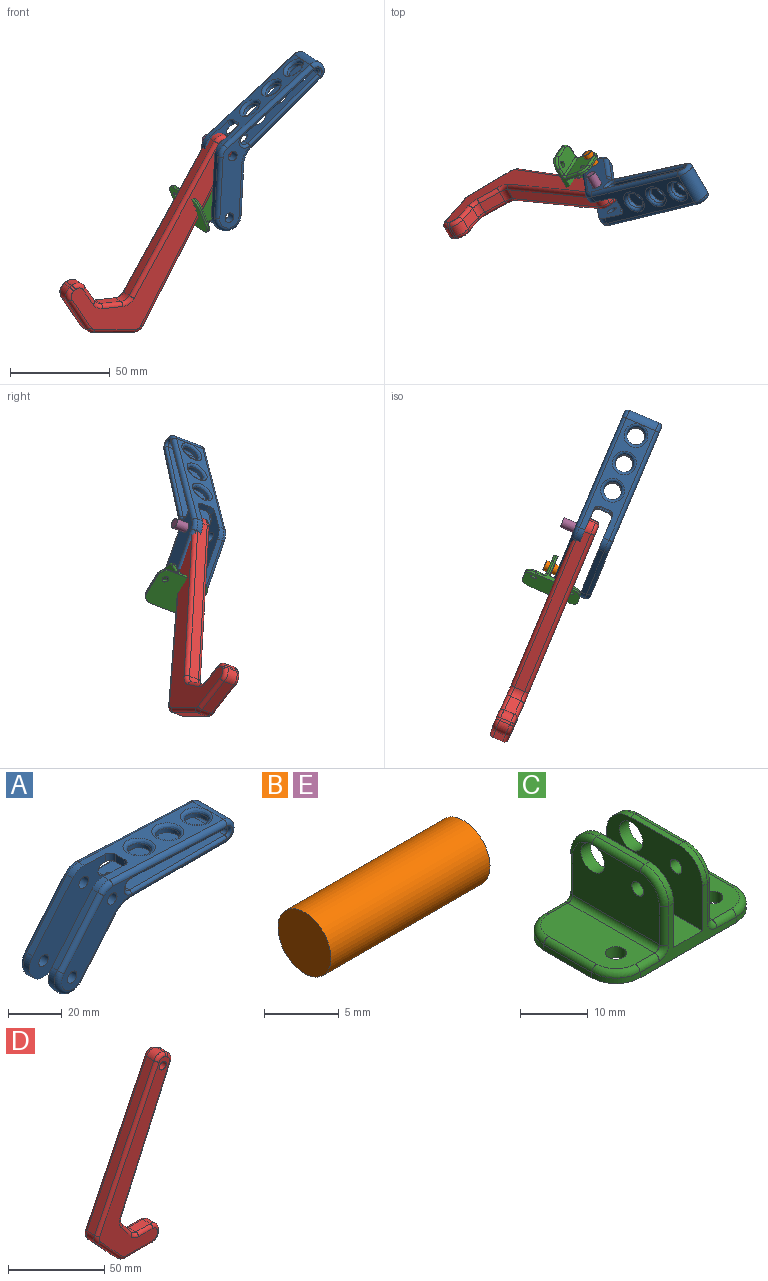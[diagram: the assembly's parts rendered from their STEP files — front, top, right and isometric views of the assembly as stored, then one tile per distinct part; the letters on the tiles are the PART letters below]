
ASSEMBLY  parts=5 mates=4
PART A: 69 faces, bbox 94.6x20x41.3 mm
  f0: plane 89.48x36mm, normal (0,-1,0), area 446.6mm2, adj f11,f13,f35,f36,f37,f38,f39,f40
  f1: plane 89.48x36mm, normal (0,1,0), area 446.6mm2, adj f21,f23,f27,f28,f29,f30,f31,f32
  f2: plane 5x3.37mm, normal (-1,0,0.04), area 16.9mm2, adj f5,f6,f16,f45
  f3: plane 40.19x40mm, normal (0,-1,0), area 673.6mm2, adj f5,f14,f16,f17,f18,f19,f20,f21
  f4: plane 40.19x40mm, normal (0,1,0), area 673.6mm2, adj f6,f7,f8,f9,f10,f11,f12,f13
  f5: cylinder r=2.5mm len=3.47mm, axis (0.04,0,1), area 13.2mm2, adj f2,f3,f16,f45
  f6: cylinder r=2.5mm len=3.47mm, axis (-0.04,0,-1), area 13.2mm2, adj f2,f4,f16,f45
  f7: cylinder r=7.5mm len=6.06mm, axis (0,1,0), area 20.6mm2, adj f4,f8,f16,f40
  f8: plane 25x20.98mm, normal (-0.77,0,0.64), area 97.9mm2, adj f4,f7,f9,f42
  f9: cylinder r=7.5mm len=13.25mm, axis (0,1,0), area 70.7mm2, adj f4,f8,f10,f41
  f10: plane 21.25x17.82mm, normal (0.77,0,-0.64), area 83.2mm2, adj f4,f9,f12,f39
  f11: cylinder r=2.5mm len=5mm, axis (0,1,0), area 78.5mm2, adj f0,f4
  f12: cylinder r=10mm len=7.66mm, axis (0,1,0), area 26.2mm2, adj f4,f10,f14,f37
  f13: cylinder r=2.5mm len=5mm, axis (0,1,0), area 78.5mm2, adj f0,f4
  f14: plane 49.79x16.04mm, normal (0,0,-1), area 424.8mm2, adj f3,f4,f12,f15,f22,f24,f25,f26
  f15: cylinder r=5mm len=16mm, axis (0,1,0), area 247.9mm2, adj f14,f16,f33,f36,f66
  f16: plane 59.9x16mm, normal (0.04,0,1), area 483.2mm2, adj f2,f3,f4,f5,f6,f7,f15,f17
  f17: cylinder r=7.5mm len=6.06mm, axis (0,1,0), area 20.6mm2, adj f3,f16,f18,f29
  f18: plane 25x20.98mm, normal (-0.77,0,0.64), area 97.9mm2, adj f3,f17,f19,f27
  f19: cylinder r=7.5mm len=13.25mm, axis (0,1,0), area 70.7mm2, adj f3,f18,f20,f28
  f20: plane 21.25x17.82mm, normal (0.77,0,-0.64), area 83.2mm2, adj f3,f19,f22,f30
  f21: cylinder r=2.5mm len=5mm, axis (0,1,0), area 78.5mm2, adj f1,f3
  f22: cylinder r=10mm len=7.66mm, axis (0,1,0), area 26.2mm2, adj f3,f14,f20,f32
  f23: cylinder r=2.5mm len=5mm, axis (0,1,0), area 78.5mm2, adj f1,f3
  f24: plane 5x3.37mm, normal (-1,0,0.04), area 16.9mm2, adj f14,f25,f26,f46
  f25: cylinder r=2.5mm len=3.58mm, axis (0.04,0,1), area 13.2mm2, adj f3,f14,f24,f46
  f26: cylinder r=2.5mm len=3.58mm, axis (-0.04,0,-1), area 13.2mm2, adj f4,f14,f24,f46
  f27: cylinder r=2mm len=26.29mm, axis (-0.64,0,-0.77), area 102.5mm2, adj f1,f18,f28,f29
  f28: torus R=5.5mm, axis (0,-1,0), area 66.9mm2, adj f1,f19,f27,f30
  f29: torus R=5.5mm, axis (0,-1,0), area 19.5mm2, adj f1,f17,f27,f31
  f30: cylinder r=2mm len=22.53mm, axis (0.64,0,0.77), area 87.1mm2, adj f1,f20,f28,f32
  f31: cylinder r=2mm len=59.98mm, axis (-1,0,0.04), area 188.3mm2, adj f1,f16,f29,f33
  f32: torus R=12mm, axis (0,-1,0), area 29.4mm2, adj f1,f22,f30,f34
  f33: torus R=3mm, axis (0,-1,0), area 41.6mm2, adj f1,f15,f31,f34
  f34: cylinder r=2mm len=49.75mm, axis (1,0,0), area 156.3mm2, adj f1,f14,f32,f33
  f35: cylinder r=2mm len=49.75mm, axis (-1,0,0), area 156.3mm2, adj f0,f14,f36,f37
  f36: torus R=3mm, axis (0,-1,0), area 41.6mm2, adj f0,f15,f35,f38
  f37: torus R=12mm, axis (0,-1,0), area 29.4mm2, adj f0,f12,f35,f39
  f38: cylinder r=2mm len=59.98mm, axis (1,0,-0.04), area 188.3mm2, adj f0,f16,f36,f40
  f39: cylinder r=2mm len=22.53mm, axis (-0.64,0,-0.77), area 87.1mm2, adj f0,f10,f37,f41
  f40: torus R=5.5mm, axis (0,-1,0), area 19.5mm2, adj f0,f7,f38,f42
  f41: torus R=5.5mm, axis (0,-1,0), area 66.9mm2, adj f0,f9,f39,f42
  f42: cylinder r=2mm len=26.29mm, axis (0.64,0,0.77), area 102.5mm2, adj f0,f8,f40,f41
  f43: cylinder r=1.63mm len=17.4mm, axis (0,-1,0), area 87.9mm2, adj f45,f46,f51,f54
  f44: cylinder r=2.67mm len=5.34mm, axis (0,-1,0), area 31.4mm2, adj f3,f45,f46,f48
  f45: plane 49.81x17.4mm, normal (-0.04,0,-1), area 641mm2, adj f2,f3,f4,f5,f6,f43,f44,f47
  f46: plane 49.9x17.44mm, normal (0,0,1), area 642.2mm2, adj f3,f4,f24,f25,f26,f43,f44,f47
  f47: cylinder r=2.67mm len=5.34mm, axis (0,-1,0), area 31.4mm2, adj f4,f45,f46,f53
  f48: torus R=3.97mm, axis (0,-1,0), area 20.4mm2, adj f1,f44,f49,f50
  f49: cylinder r=1.3mm len=49.86mm, axis (1,0,0), area 101.8mm2, adj f1,f46,f48,f51
  f50: cylinder r=1.3mm len=49.87mm, axis (-1,0,0.04), area 101.8mm2, adj f1,f45,f48,f51
  f51: torus R=2.93mm, axis (0,-1,0), area 13.3mm2, adj f1,f43,f49,f50
  f52: cylinder r=1.3mm len=49.87mm, axis (1,0,-0.04), area 101.8mm2, adj f0,f45,f53,f54
  f53: torus R=3.97mm, axis (0,-1,0), area 20.4mm2, adj f0,f47,f52,f55
  f54: torus R=2.93mm, axis (0,-1,0), area 13.3mm2, adj f0,f43,f52,f55
  f55: cylinder r=1.3mm len=49.86mm, axis (-1,0,0), area 101.8mm2, adj f0,f46,f53,f54
  f56: cylinder r=4.5mm len=9mm, axis (0,0,-1), area 52.9mm2, adj f46,f65,f66
  f57: cylinder r=4.5mm len=9mm, axis (0,0,-1), area 52.9mm2, adj f46,f67
  f58: cylinder r=4.5mm len=9mm, axis (0,0,-1), area 52.9mm2, adj f46,f68
  f59: cylinder r=4.5mm len=9mm, axis (0,0,-1), area 52.9mm2, adj f45,f64
  f60: cylinder r=4.5mm len=9mm, axis (0,0,-1), area 52.9mm2, adj f45,f63
  f61: cylinder r=4.5mm len=9mm, axis (0,0,-1), area 52.9mm2, adj f45,f62
  f62: bspline ~12x12mm, area 74.7mm2, adj f16,f61
  f63: bspline ~11.99x11.99mm, area 74.7mm2, adj f16,f60
  f64: bspline ~11.99x11.99mm, area 74.7mm2, adj f16,f59
  f65: torus R=6mm, axis (0,0,1), area 71.5mm2, adj f14,f56,f66
  f66: bspline ~3.89x1.77mm, area 3.2mm2, adj f15,f56,f65
  f67: torus R=6mm, axis (0,0,1), area 74.7mm2, adj f14,f57
  f68: torus R=6mm, axis (0,0,1), area 74.7mm2, adj f14,f58
PART B: 3 faces, bbox 15x5x5 mm
  f0: cylinder r=2.5mm len=15mm, axis (-1,0,0), area 235.6mm2, adj f1,f2
  f1: plane 5x5mm, normal (1,0,0), area 19.6mm2, adj f0
  f2: plane 5x5mm, normal (-1,0,0), area 19.6mm2, adj f0
PART C: 54 faces, bbox 30.8x20.8x15.4 mm
  f0: plane 18x8mm, normal (0,0,1), area 129.1mm2, adj f24,f25,f26,f27,f28,f29,f51
  f1: plane 10x1mm, normal (-1,0,0), area 10mm2, adj f2,f21,f23,f24
  f2: plane 30x20mm, normal (0,0,-1), area 562.5mm2, adj f1,f3,f12,f13,f20,f21,f22,f23
  f3: plane 10x1mm, normal (1,0,0), area 10mm2, adj f2,f20,f22,f37
  f4: plane 18x8mm, normal (0,0,1), area 129.1mm2, adj f37,f38,f39,f40,f41,f42,f50
  f5: plane 18x11mm, normal (1,0,0), area 167.9mm2, adj f15,f42,f45,f46,f47,f48,f49,f53
  f6: plane 10x1mm, normal (0,0,1), area 10mm2, adj f7,f17,f19,f49
  f7: plane 20x13mm, normal (-1,0,0), area 225.9mm2, adj f6,f8,f12,f13,f15,f17,f19,f53
  f8: plane 20x6mm, normal (0,0,1), area 120mm2, adj f7,f9,f12,f13
  f9: plane 20x13mm, normal (1,0,0), area 225.9mm2, adj f8,f10,f12,f13,f14,f16,f18,f52
  f10: plane 10x1mm, normal (0,0,1), area 10mm2, adj f9,f16,f18,f36
  f11: plane 18x11mm, normal (-1,0,0), area 167.9mm2, adj f14,f28,f32,f33,f34,f35,f36,f52
  f12: plane 20x10mm, normal (0,-1,0), area 45.7mm2, adj f2,f7,f8,f9,f16,f17,f22,f23
  f13: plane 20x10mm, normal (0,1,0), area 45.7mm2, adj f2,f7,f8,f9,f18,f19,f20,f21
  f14: cylinder r=2.45mm len=4.9mm, axis (-1,0,0), area 30.8mm2, adj f9,f11,f35,f36
  f15: cylinder r=2.45mm len=4.9mm, axis (-1,0,0), area 30.8mm2, adj f5,f7,f48,f49
  f16: cylinder r=5mm len=5mm, axis (1,0,0), area 7.9mm2, adj f9,f10,f12,f34
  f17: cylinder r=5mm len=5mm, axis (1,0,0), area 7.9mm2, adj f6,f7,f12,f47
  f18: cylinder r=5mm len=5mm, axis (-1,0,0), area 7.9mm2, adj f9,f10,f13,f35
  f19: cylinder r=5mm len=5mm, axis (-1,0,0), area 7.9mm2, adj f6,f7,f13,f48
  f20: cylinder r=5mm len=5mm, axis (0,0,1), area 7.9mm2, adj f2,f3,f13,f39
  f21: cylinder r=5mm len=5mm, axis (0,0,-1), area 7.9mm2, adj f1,f2,f13,f26
  f22: cylinder r=5mm len=5mm, axis (0,0,-1), area 7.9mm2, adj f2,f3,f12,f38
  f23: cylinder r=5mm len=5mm, axis (0,0,1), area 7.9mm2, adj f1,f2,f12,f25
  f24: cylinder r=1mm len=10mm, axis (0,1,0), area 15.7mm2, adj f0,f1,f25,f26
  f25: torus R=4mm, axis (0,0,1), area 11.4mm2, adj f0,f23,f24,f27
  f26: torus R=4mm, axis (0,0,1), area 11.4mm2, adj f0,f21,f24,f29
  f27: cylinder r=1mm len=4mm, axis (1,0,0), area 6.3mm2, adj f0,f12,f25,f30
  f28: cylinder r=1mm len=18mm, axis (0,-1,0), area 28.3mm2, adj f0,f11,f30,f31
  f29: cylinder r=1mm len=4mm, axis (-1,0,0), area 6.3mm2, adj f0,f13,f26,f31
  f30: torus R=2mm, axis (0,-1,0), area 3.4mm2, adj f12,f27,f28,f32
  f31: torus R=2mm, axis (0,-1,0), area 3.4mm2, adj f13,f28,f29,f33
  f32: cylinder r=1mm len=7mm, axis (0,0,1), area 11mm2, adj f11,f12,f30,f34
  f33: cylinder r=1mm len=7mm, axis (0,0,-1), area 11mm2, adj f11,f13,f31,f35
  f34: torus R=4mm, axis (-1,0,0), area 11.4mm2, adj f11,f16,f32,f36
  f35: torus R=4mm, axis (-1,0,0), area 11.4mm2, adj f11,f14,f18,f33,f36
  f36: cylinder r=1mm len=10mm, axis (0,1,0), area 15.6mm2, adj f10,f11,f14,f34,f35
  f37: cylinder r=1mm len=10mm, axis (0,1,0), area 15.7mm2, adj f3,f4,f38,f39
  f38: torus R=4mm, axis (0,0,-1), area 11.4mm2, adj f4,f22,f37,f40
  f39: torus R=4mm, axis (0,0,-1), area 11.4mm2, adj f4,f20,f37,f41
  f40: cylinder r=1mm len=4mm, axis (1,0,0), area 6.3mm2, adj f4,f12,f38,f43
  f41: cylinder r=1mm len=4mm, axis (-1,0,0), area 6.3mm2, adj f4,f13,f39,f44
  f42: cylinder r=1mm len=18mm, axis (0,-1,0), area 28.3mm2, adj f4,f5,f43,f44
  f43: torus R=2mm, axis (0,-1,0), area 3.4mm2, adj f12,f40,f42,f45
  f44: torus R=2mm, axis (0,-1,0), area 3.4mm2, adj f13,f41,f42,f46
  f45: cylinder r=1mm len=7mm, axis (0,0,-1), area 11mm2, adj f5,f12,f43,f47
  f46: cylinder r=1mm len=7mm, axis (0,0,1), area 11mm2, adj f5,f13,f44,f48
  f47: torus R=4mm, axis (-1,0,0), area 11.4mm2, adj f5,f17,f45,f49
  f48: torus R=4mm, axis (-1,0,0), area 11.4mm2, adj f5,f15,f19,f46,f49
  f49: cylinder r=1mm len=10mm, axis (0,1,0), area 15.6mm2, adj f5,f6,f15,f47,f48
  f50: cylinder r=1.6mm len=3.2mm, axis (0,0,-1), area 20.1mm2, adj f2,f4
  f51: cylinder r=1.6mm len=3.2mm, axis (0,0,-1), area 20.1mm2, adj f0,f2
  f52: cylinder r=1.2mm len=2.4mm, axis (1,0,0), area 15.1mm2, adj f9,f11
  f53: cylinder r=1.2mm len=2.4mm, axis (1,0,0), area 15.1mm2, adj f5,f7
PART D: 51 faces, bbox 56.5x9.5x117.6 mm
  f0: plane 5.5x1.43mm, normal (1,0,0), area 7.9mm2, adj f1,f16,f30,f49
  f1: cylinder r=5.08mm len=5.5mm, axis (0,1,0), area 43.9mm2, adj f0,f2,f32,f47
  f2: plane 10.53x5.5mm, normal (0,0,1), area 57.9mm2, adj f1,f3,f34,f45
  f3: cylinder r=5.08mm len=5.5mm, axis (0,1,0), area 25.6mm2, adj f2,f4,f33,f43
  f4: plane 9.18x7.03mm, normal (0.79,0,0.61), area 63.6mm2, adj f3,f5,f31,f41
  f5: cylinder r=5.08mm len=5.5mm, axis (0,1,0), area 30mm2, adj f4,f6,f29,f39
  f6: plane 80.63x36.01mm, normal (0.91,0,-0.41), area 485.7mm2, adj f5,f7,f27,f37
  f7: cylinder r=5.08mm len=6.48mm, axis (0,1,0), area 41.1mm2, adj f6,f8,f25,f35
  f8: plane 5.5x1.91mm, normal (0.5,0,0.87), area 12.1mm2, adj f7,f9,f23,f36
  f9: cylinder r=5.08mm len=7.1mm, axis (0,1,0), area 45.8mm2, adj f8,f10,f21,f38
  f10: plane 89.34x43.6mm, normal (-0.9,0,0.44), area 546.7mm2, adj f9,f11,f19,f40
  f11: cylinder r=5.08mm len=5.69mm, axis (0,1,0), area 33.6mm2, adj f10,f12,f20,f42
  f12: plane 17.31x16.12mm, normal (-0.73,0,-0.68), area 130.1mm2, adj f11,f13,f22,f44
  f13: cylinder r=5.08mm len=5.5mm, axis (0,1,0), area 22.9mm2, adj f12,f14,f24,f46
  f14: plane 20.22x5.5mm, normal (0,0,-1), area 111.2mm2, adj f13,f16,f26,f48
  f15: cylinder r=2.5mm len=9.5mm, axis (0,1,0), area 149.2mm2, adj f17,f18
  f16: cylinder r=5.08mm len=5.5mm, axis (0,1,0), area 43.9mm2, adj f0,f14,f28,f50
  f17: plane 112.81x51.67mm, normal (0,-1,0), area 1401.9mm2, adj f15,f19,f20,f21,f22,f23,f24,f25
  f18: plane 112.81x51.67mm, normal (0,1,0), area 1401.9mm2, adj f15,f35,f36,f37,f38,f39,f40,f41
  f19: cylinder r=2mm len=90.22mm, axis (0.44,0,0.9), area 312.3mm2, adj f10,f17,f20,f21
  f20: torus R=3.08mm, axis (0,-1,0), area 16.5mm2, adj f11,f17,f19,f22
  f21: torus R=3.08mm, axis (0,-1,0), area 22.4mm2, adj f9,f17,f19,f23
  f22: cylinder r=2mm len=18.67mm, axis (-0.68,0,0.73), area 74.3mm2, adj f12,f17,f20,f24
  f23: cylinder r=2mm len=2.91mm, axis (0.87,0,-0.5), area 6.9mm2, adj f8,f17,f21,f25
  f24: torus R=3.08mm, axis (0,-1,0), area 11.2mm2, adj f13,f17,f22,f26
  f25: torus R=3.08mm, axis (0,-1,0), area 20.1mm2, adj f7,f17,f23,f27
  f26: cylinder r=2mm len=20.22mm, axis (-1,0,0), area 63.5mm2, adj f14,f17,f24,f28
  f27: cylinder r=2mm len=81.45mm, axis (-0.41,0,-0.91), area 277.4mm2, adj f6,f17,f25,f29
  f28: torus R=3.08mm, axis (0,-1,0), area 21.5mm2, adj f16,f17,f26,f30
  f29: torus R=7.08mm, axis (0,-1,0), area 19.6mm2, adj f5,f17,f27,f31
  f30: cylinder r=2mm len=2mm, axis (0,0,-1), area 4.5mm2, adj f0,f17,f28,f32
  f31: cylinder r=2mm len=10.4mm, axis (0.61,0,-0.79), area 36.3mm2, adj f4,f17,f29,f33
  f32: torus R=3.08mm, axis (0,-1,0), area 21.5mm2, adj f1,f17,f30,f34
  f33: torus R=7.08mm, axis (0,-1,0), area 16.7mm2, adj f3,f17,f31,f34
  f34: cylinder r=2mm len=10.53mm, axis (1,0,0), area 33.1mm2, adj f2,f17,f32,f33
  f35: torus R=3.08mm, axis (0,-1,0), area 20.1mm2, adj f7,f18,f36,f37
  f36: cylinder r=2mm len=2.91mm, axis (-0.87,0,0.5), area 6.9mm2, adj f8,f18,f35,f38
  f37: cylinder r=2mm len=81.45mm, axis (0.41,0,0.91), area 277.4mm2, adj f6,f18,f35,f39
  f38: torus R=3.08mm, axis (0,-1,0), area 22.4mm2, adj f9,f18,f36,f40
  f39: torus R=7.08mm, axis (0,-1,0), area 19.6mm2, adj f5,f18,f37,f41
  f40: cylinder r=2mm len=90.22mm, axis (-0.44,0,-0.9), area 312.3mm2, adj f10,f18,f38,f42
  f41: cylinder r=2mm len=10.4mm, axis (-0.61,0,0.79), area 36.3mm2, adj f4,f18,f39,f43
  f42: torus R=3.08mm, axis (0,-1,0), area 16.5mm2, adj f11,f18,f40,f44
  f43: torus R=7.08mm, axis (0,-1,0), area 16.7mm2, adj f3,f18,f41,f45
  f44: cylinder r=2mm len=18.67mm, axis (0.68,0,-0.73), area 74.3mm2, adj f12,f18,f42,f46
  f45: cylinder r=2mm len=10.53mm, axis (-1,0,0), area 33.1mm2, adj f2,f18,f43,f47
  f46: torus R=3.08mm, axis (0,-1,0), area 11.2mm2, adj f13,f18,f44,f48
  f47: torus R=3.08mm, axis (0,-1,0), area 21.5mm2, adj f1,f18,f45,f49
  f48: cylinder r=2mm len=20.22mm, axis (1,0,0), area 63.5mm2, adj f14,f18,f46,f50
  f49: cylinder r=2mm len=2mm, axis (0,0,1), area 4.5mm2, adj f0,f18,f47,f50
  f50: torus R=3.08mm, axis (0,-1,0), area 21.5mm2, adj f16,f18,f48,f49
PART E: same geometry as B
PLACE A rot(axis=(0.53,-0.75,0.39),54.3deg) t=(63.62,-98.37,-16.55)mm
PLACE B rot(axis=(-0.56,0.58,-0.59),75.8deg) t=(27.81,-92.15,-66.07)mm
PLACE C rot(axis=(-0.56,0.58,-0.59),75.8deg) t=(33.11,-102.18,-55.39)mm
PLACE D rot(axis=(-0.44,0.04,-0.9),145.1deg) t=(15.09,-120.02,-68.65)mm
PLACE E rot(axis=(0.35,0.29,0.89),133.6deg) t=(24.52,-131.01,-17.1)mm
MATE slider B.f0 <-> C.f14  axis (0.48,-0.82,-0.31) through (44.57,-107.57,-47.68)mm
MATE cylindrical A.f9 <-> C.f14  axis (0.48,-0.82,-0.31) through (50.39,-117.4,-51.41)mm
MATE slider D.f15 <-> E.f0  axis (0.48,-0.82,-0.31) through (47.39,-120.3,-17.66)mm
MATE cylindrical E.f0 <-> A.f7  axis (-0.48,0.82,0.31) through (38.94,-106,-12.22)mm
